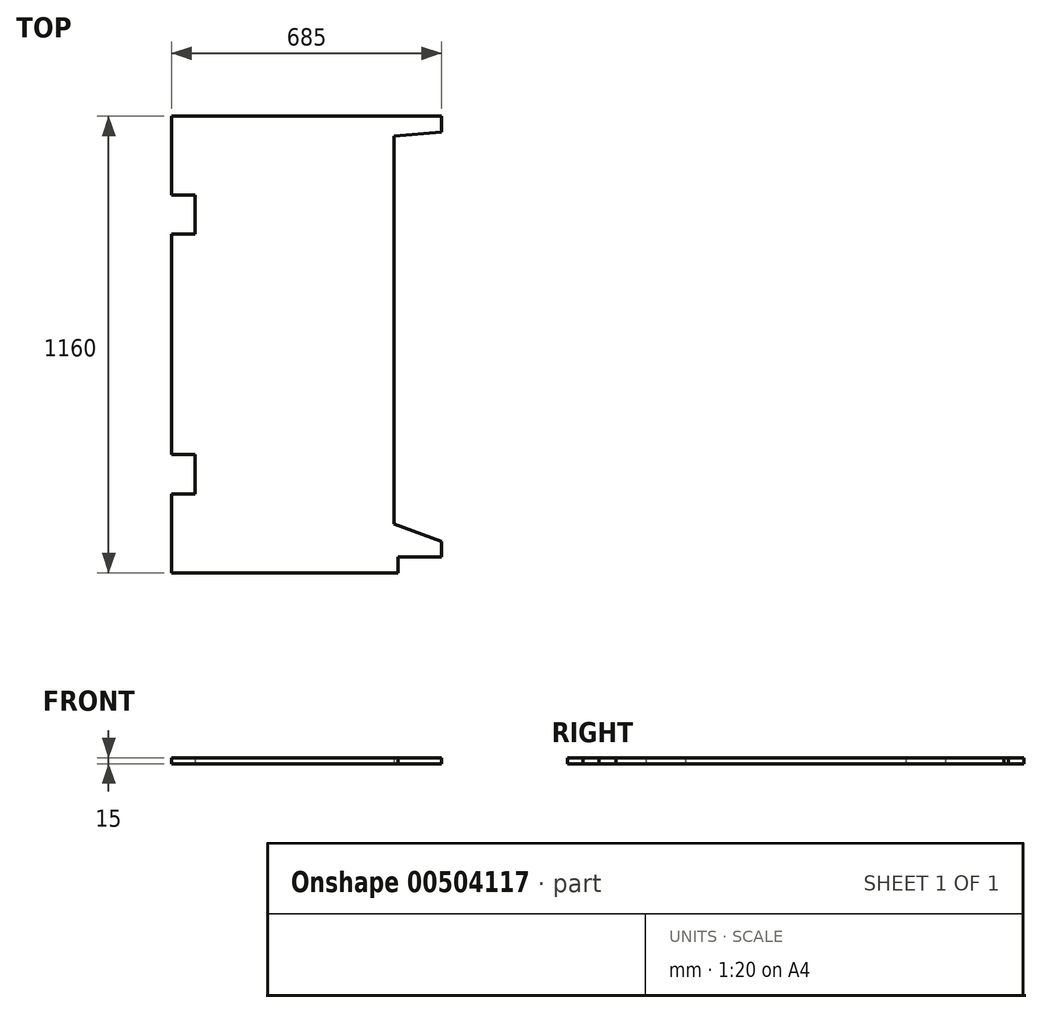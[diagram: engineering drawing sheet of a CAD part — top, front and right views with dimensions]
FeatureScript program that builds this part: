
annotation { "Feature Type Name" : "Feature", "Feature Type Description" : "" }
export const myFeature = defineFeature(function(context is Context, id is Id, definition is map)
    precondition{}
    {
        {
            var Q0;
            Q0=qCreatedBy(makeId("Top.planeOp"),FACE);
            var sketch = newSketch(context, id + "F0", { "sketchPlane" : qUnion([Q0])});
            skLineSegment(sketch, "E0", {"start": v(0, 0) * mm, "end": v(575, 0) * mm});
            skLineSegment(sketch, "E1", {"start": v(575, 0) * mm, "end": v(575, 40) * mm});
            skLineSegment(sketch, "E2", {"start": v(685, 40) * mm, "end": v(575, 40) * mm});
            skLineSegment(sketch, "E3", {"start": v(685, 40) * mm, "end": v(685, 80) * mm});
            skLineSegment(sketch, "E4", {"start": v(565, 123.68) * mm, "end": v(685, 80) * mm});
            skLineSegment(sketch, "E5", {"start": v(565, 123.68) * mm, "end": v(565, 1109.5) * mm});
            skLineSegment(sketch, "E6", {"start": v(565, 1109.5) * mm, "end": v(685, 1120) * mm});
            skLineSegment(sketch, "E7", {"start": v(685, 1120) * mm, "end": v(685, 1160) * mm});
            skLineSegment(sketch, "E8", {"start": v(685, 1160) * mm, "end": v(0, 1160) * mm});
            skLineSegment(sketch, "E9", {"start": v(0, 1160) * mm, "end": v(0, 960) * mm});
            skLineSegment(sketch, "E10", {"start": v(0, 960) * mm, "end": v(60, 960) * mm});
            skLineSegment(sketch, "E11", {"start": v(60, 960) * mm, "end": v(60, 860) * mm});
            skLineSegment(sketch, "E12", {"start": v(60, 860) * mm, "end": v(0, 860) * mm});
            skLineSegment(sketch, "E13", {"start": v(0, 860) * mm, "end": v(0, 300) * mm});
            skLineSegment(sketch, "E14", {"start": v(0, 300) * mm, "end": v(60, 300) * mm});
            skLineSegment(sketch, "E15", {"start": v(60, 300) * mm, "end": v(60, 200) * mm});
            skLineSegment(sketch, "E16", {"start": v(60, 200) * mm, "end": v(0, 200) * mm});
            skLineSegment(sketch, "E17", {"start": v(0, 200) * mm, "end": v(0, 0) * mm});
            skSolve(sketch);
        }
        {
            var Q0;
            Q0=makeQuery(id+"F0.imprint","IMPRINT",FACE,{"disambiguationData":[TD([[makeQuery(id+"F0.imprint","IMPRINT",EDGE,{"derivedFrom":sQuery(id+"F0.wireOp",EDGE,"E0")}),1.0]])]});
            extrude(context, id + "F1", {"entities" : qUnion([Q0]), "depth" : 15 * mm});
        }
    });
